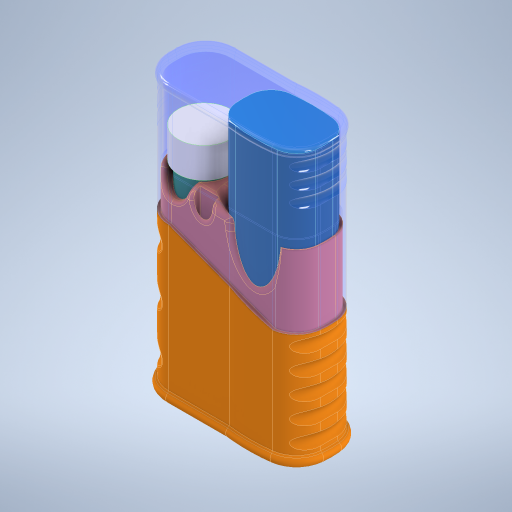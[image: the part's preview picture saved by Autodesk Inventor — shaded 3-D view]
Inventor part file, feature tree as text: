
AUTODESK INVENTOR PART (.ipt)
format: ipt  version: 2023 (Build 270158030, 158C)  size: 1,740,800 bytes
history: native  units: mm
features: sketch x22, extrude x19, fillet x14, projected_geometry x13, other x5, revolve x4, plane x1, sweep x1
ambient origin geometry x8: Origin, YZ Plane, XZ Plane, XY Plane, X Axis, Y Axis, Z Axis, Center Point
bodies: Body1 (feature_tree), Body2 (feature_tree), Body3 (feature_tree), Body4 (feature_tree)
feature tree (79):
  other  "vape"
  extrude  "Extrusion1"  Depth=8.35mm
  fillet  "Fillet1"  Radius=70.0mm
  extrude  "Extrusion2"  Depth=11.6mm TaperAngle=0.0deg
  plane  "Work Plane1"
  extrude  "Extrusion3"  Depth=45.8mm TaperAngle=0.0deg
  extrude  "Extrusion4"  Depth=22.1mm
  extrude  "Extrusion5"  Depth=1.5mm
  extrude  "Extrusion6"  Depth=1.5mm
  fillet  "Fillet2"  Radius=1.5mm
  extrude  "Extrusion8"  Depth=15.55mm
  extrude  "Extrusion20"  Depth=3.0mm
  extrude  "Extrusion21"  Depth=3.0mm
  sweep  "Sweep2"
  sketch  "Sketch26"  dims[d105=71.0mm d106=0.0mm d108=71.0mm d109=0.0mm d110=3.0mm d111=30.0deg]
  extrude  "Extrusion22"  Depth=13.0mm
  fillet  "Fillet22"  Radius=2.0mm
  fillet  "Fillet23"  Radius=10.0mm
  fillet  "Fillet24"  Radius=11.0mm
  fillet  "Fillet25"  Radius=4.0mm
  fillet  "Fillet26"  Radius=2.0mm
  fillet  "Fillet4"  Radius=2.9mm
  extrude  "Extrusion10"  Depth=2.4mm
  extrude  "Extrusion11"  Depth=7.0mm
  fillet  "Fillet10"  Radius=45.0mm
  fillet  "Fillet27"  Radius=0.25mm
  extrude  "Extrusion13"  Depth=71.0mm TaperAngle=0.0deg
  fillet  "Fillet28"  Radius=3.0mm
  sketch  "Sketch14"  dims[d50=3.0mm d51=3.0mm]
  extrude  "Extrusion14"  Depth=15.0mm TaperAngle=0.0deg
  extrude  "Extrusion23"  TaperAngle=0.0deg  [1 undecoded]
  extrude  "Extrusion24"  Depth=15.0mm
  extrude  "Extrusion15"  Depth=20.0mm
  fillet  "Fillet29"  Radius=9.0mm
  extrude  "Extrusion25"  Depth=6.0mm
  fillet  "Fillet30"  Radius=4.0mm
  other  "Work Axis1"
  revolve  "Revolution1"  [1 undecoded]
  sketch  "Sketch30"  dims[d172=15.780931mm d173=20.0mm d174=9.0mm]
  revolve  "Revolution2"  [1 undecoded]
  fillet  "Fillet32"  Radius=1.0mm
  extrude  "Extrusion26"  Depth=24.0mm
  sketch  "Sketch35"  dims[d178=1.0mm d179=2.0mm]
  revolve  "Revolution3"  [1 undecoded]
  revolve  "Revolution5"  [1 undecoded]
  sketch  "Sketch1"  dims[d4=98.5mm d5=0.0mm d9=8.35mm d22=70.0mm d23=0.0mm]
  sketch  "Sketch2"  dims[d24=20.0mm d26=11.6mm d27=0.0mm]
  other  "vape-tube"
  sketch  "Sketch3"  dims[d28=17.0mm d29=45.8mm d30=0.0mm]
  other  "storage"
  sketch  "Sketch4"  dims[d31=17.0mm d38=22.1mm]
  sketch  "Sketch5"  dims[d39=31.1mm d41=1.5mm]
  projected_geometry  "Projected Loop2"
  sketch  "Sketch6"  dims[d42=1.5mm d44=1.5mm d45=1.5mm]
  projected_geometry  "Projected Loop3"
  projected_geometry  "Projected Loop4"
  sketch  "Sketch8"  dims[d46=11.05mm d47=15.55mm]
  projected_geometry  "Projected Loop6"
  sketch  "Sketch11"  dims[d48=3.0mm d49=3.0mm]
  sketch  "Sketch15"  dims[d52=11.05mm d53=15.55mm]
  other  "vape-lid"
  sketch  "Sketch22"  dims[d54=2.0mm d55=13.0mm]
  projected_geometry  "Projected Loop13"
  sketch  "Sketch23"  dims[d56=12.5mm d57=60.0mm d58=0.0mm d59=2.0mm d60=10.0mm d61=0.0mm d62=11.0mm d66=4.0mm d67=8.726646mm d69=2.0mm d83=2.9mm]
  projected_geometry  "Projected Loop14"
  sketch  "Sketch24"  dims[d86=72.0mm d87=0.0mm d88=2.4mm]
  sketch  "Sketch25"  dims[d89=7.3mm d91=7.0mm d92=45.0mm d93=0.0mm d94=0.25mm]
  sketch  "Sketch27"  dims[d158=1.0mm d159=15.0mm d160=0.0mm]
  projected_geometry  "Projected Loop15"
  projected_geometry  "Projected Loop16"
  projected_geometry  "Projected Loop17"
  projected_geometry  "Projected Loop18"
  projected_geometry  "Projected Loop19"
  projected_geometry  "Projected Loop20"
  sketch  "Sketch28"  dims[d161=15.0mm d162=0.0mm d163=0.0mm d164=0.0mm]
  sketch  "Sketch29"  dims[d169=0.0mm d170=0.0mm d171=15.0mm]
  sketch  "Sketch33"  dims[d175=7.5mm d176=6.0mm d177=4.0mm]
  projected_geometry  "Projected Loop31"
  sketch  "Sketch37"  dims[d180=1.2mm d181=0.5mm d182=1.0mm d183=24.0mm d184=2.0mm d185=0.5mm d186=2.35mm d187=4.0mm d188=0.5mm d189=10.0mm d190=0.0mm d191=10.0mm d192=0.0mm d193=1.5mm d194=6.0mm d195=3.65mm d196=10.0mm d197=0.0mm d198=2.5mm d199=14.0mm d200=19.0mm d201=19.0mm d207=180.0deg d208=8.0mm d209=8.0mm d210=8.0mm d211=8.0mm d212=8.0mm d213=12.5mm d214=4.0mm d215=0.0mm d216=180.0deg d218=1.5mm d220=0.5mm d221=27.75mm d222=0.0mm d223=8.0mm d224=4.0mm d225=6.0mm d226=6.0mm d227=11.5mm d228=6.0mm d229=6.0mm d230=180.0deg d240=2.9mm d241=6.0mm d242=6.0mm d243=6.0mm d244=41.5mm d245=11.5mm d246=6.0mm d247=180.0deg d249=20.0mm d253=22.0mm d254=22.0mm d255=25.0mm]
note: 5 required parameter values undecoded (feature->parameter linkage not recoverable at this tier; creation-order binding heuristic only, values carry confidence <= 0.55)